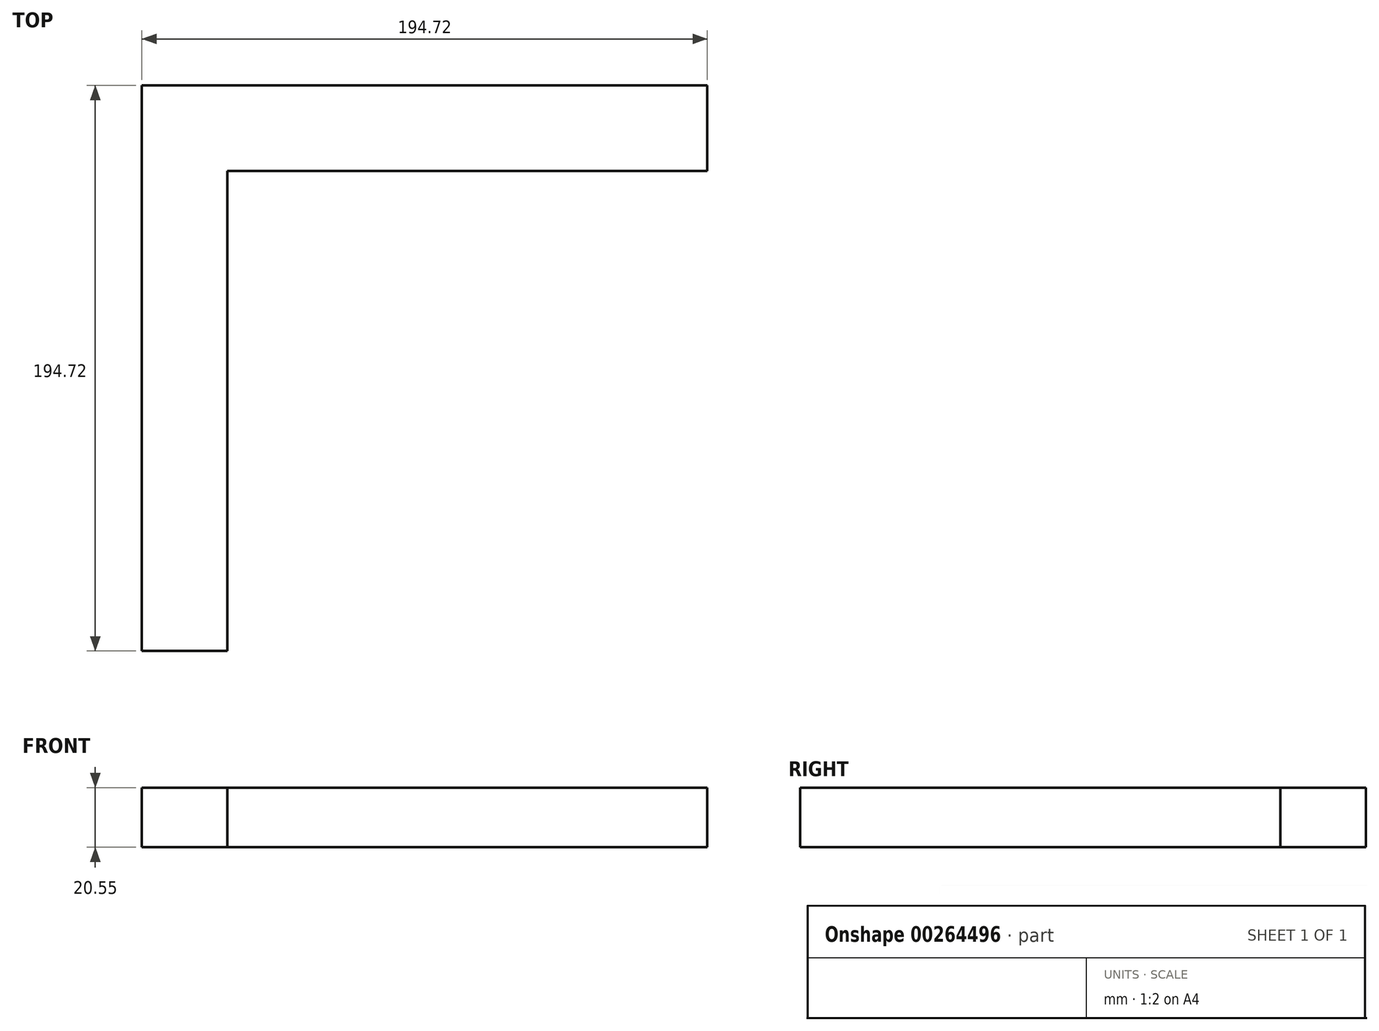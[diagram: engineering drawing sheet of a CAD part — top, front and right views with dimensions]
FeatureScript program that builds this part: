
annotation { "Feature Type Name" : "Feature", "Feature Type Description" : "" }
export const myFeature = defineFeature(function(context is Context, id is Id, definition is map)
    precondition{}
    {
        {
            var Q0;
            Q0=qCreatedBy(makeId("Top.planeOp"),FACE);
            var sketch = newSketch(context, id + "F0", { "sketchPlane" : qUnion([Q0])});
            skLineSegment(sketch, "E0.bottom", {"start": v(-89.62, 89.63) * mm, "end": v(89.63, 89.63) * mm, "construction": true});
            skLineSegment(sketch, "E0.top", {"start": v(-89.62, -89.63) * mm, "end": v(89.63, -89.63) * mm, "construction": true});
            skLineSegment(sketch, "E0.left", {"start": v(-89.62, 89.62) * mm, "end": v(-89.62, -89.63) * mm, "construction": true});
            skLineSegment(sketch, "E0.right", {"start": v(89.62, 89.63) * mm, "end": v(89.62, -89.63) * mm, "construction": true});
            skLineSegment(sketch, "E1", {"start": v(-89.62, 0) * mm, "end": v(89.62, 0) * mm, "construction": true});
            skLineSegment(sketch, "E2", {"start": v(0, -89.63) * mm, "end": v(0, 89.63) * mm, "construction": true});
            skLineSegment(sketch, "E3", {"start": v(89.63, 60.23) * mm, "end": v(89.63, 89.63) * mm});
            skLineSegment(sketch, "E4", {"start": v(-89.62, 89.63) * mm, "end": v(-89.62, -89.63) * mm});
            skLineSegment(sketch, "E5", {"start": v(-60.23, -89.63) * mm, "end": v(-60.23, 60.23) * mm});
            skLineSegment(sketch, "E6", {"start": v(-60.23, 60.23) * mm, "end": v(89.62, 60.23) * mm});
            skLineSegment(sketch, "E7", {"start": v(-89.62, -89.63) * mm, "end": v(-60.23, -89.63) * mm});
            skLineSegment(sketch, "E8", {"start": v(-89.62, 89.63) * mm, "end": v(89.63, 89.63) * mm});
            skSolve(sketch);
        }
        {
            var Q0;
            Q0 = qSketchRegion(id + "F0", true);
            extrude(context, id + "F1", {"entities" : qUnion([Q0]), "depth" : 20.55 * mm});
        }
        {
            var Q0;
            Q0=makeQuery(id+"F1.opExtrude","CAP_FACE",FACE,{"disambiguationData":[OSD([sQuery(id+"F0.wireOp",EDGE,"E3"),sQuery(id+"F0.wireOp",EDGE,"E4"),sQuery(id+"F0.wireOp",EDGE,"E5"),sQuery(id+"F0.wireOp",EDGE,"E6"),sQuery(id+"F0.wireOp",EDGE,"E7"),sQuery(id+"F0.wireOp",EDGE,"E8")])],"isStart":false});
            var sketch = newSketch(context, id + "F2", { "sketchPlane" : qUnion([Q0])});
            skLineSegment(sketch, "E9.bottom", {"start": v(89.63, 89.63) * mm, "end": v(75.1, 89.63) * mm});
            skLineSegment(sketch, "E9.top", {"start": v(89.63, 60.23) * mm, "end": v(75.1, 60.23) * mm});
            skLineSegment(sketch, "E9.left", {"start": v(89.63, 89.63) * mm, "end": v(89.63, 60.23) * mm});
            skLineSegment(sketch, "E9.right", {"start": v(75.1, 89.63) * mm, "end": v(75.1, 60.23) * mm});
            skLineSegment(sketch, "E10.bottom", {"start": v(-89.62, -89.63) * mm, "end": v(-60.23, -89.63) * mm});
            skLineSegment(sketch, "E10.top", {"start": v(-89.62, -75.1) * mm, "end": v(-60.23, -75.1) * mm});
            skLineSegment(sketch, "E10.left", {"start": v(-89.62, -89.63) * mm, "end": v(-89.62, -75.1) * mm});
            skLineSegment(sketch, "E10.right", {"start": v(-60.23, -89.63) * mm, "end": v(-60.23, -75.1) * mm});
            skSolve(sketch);
        }
        {
            var Q0;
            Q0 = qSketchRegion(id + "F2", true);
            extrude(context, id + "F3", {"entities" : qUnion([Q0]), "operationType" : NewBodyOperationType.REMOVE, "endBound" : BoundingType.THROUGH_ALL, "oppositeDirection" : true, "depth" : 25 * mm});
        }
        {
            var Q0;
            Q0=qCreatedBy(makeId("Top.planeOp"),FACE);
            var sketch = newSketch(context, id + "F4", { "sketchPlane" : qUnion([Q0])});
            skLineSegment(sketch, "E11.bottom", {"start": v(-89.62, -75.1) * mm, "end": v(-60.23, -75.1) * mm});
            skLineSegment(sketch, "E11.top", {"start": v(-89.62, -105.1) * mm, "end": v(-60.23, -105.1) * mm});
            skLineSegment(sketch, "E11.left", {"start": v(-89.62, -75.1) * mm, "end": v(-89.62, -105.1) * mm});
            skLineSegment(sketch, "E11.right", {"start": v(-60.23, -75.1) * mm, "end": v(-60.23, -105.1) * mm});
            skLineSegment(sketch, "E12.bottom", {"start": v(75.1, 60.23) * mm, "end": v(105.1, 60.23) * mm});
            skLineSegment(sketch, "E12.top", {"start": v(75.1, 89.63) * mm, "end": v(105.1, 89.63) * mm});
            skLineSegment(sketch, "E12.left", {"start": v(75.1, 60.23) * mm, "end": v(75.1, 89.63) * mm});
            skLineSegment(sketch, "E12.right", {"start": v(105.1, 60.23) * mm, "end": v(105.1, 89.63) * mm});
            skSolve(sketch);
        }
        {
            var Q0;
            Q0 = qSketchRegion(id + "F4", true);
            var Q1;
            Q1=makeQuery(id+"F1.opExtrude","CAP_FACE",FACE,{"disambiguationData":[OSD([sQuery(id+"F0.wireOp",EDGE,"E3"),sQuery(id+"F0.wireOp",EDGE,"E4"),sQuery(id+"F0.wireOp",EDGE,"E5"),sQuery(id+"F0.wireOp",EDGE,"E6"),sQuery(id+"F0.wireOp",EDGE,"E7"),sQuery(id+"F0.wireOp",EDGE,"E8")])],"isStart":false});
            extrude(context, id + "F5", {"entities" : qUnion([Q0]), "operationType" : NewBodyOperationType.ADD, "endBound" : BoundingType.UP_TO_SURFACE, "endBoundEntityFace" : qUnion([Q1]), "depth" : 25 * mm});
        }
    });
